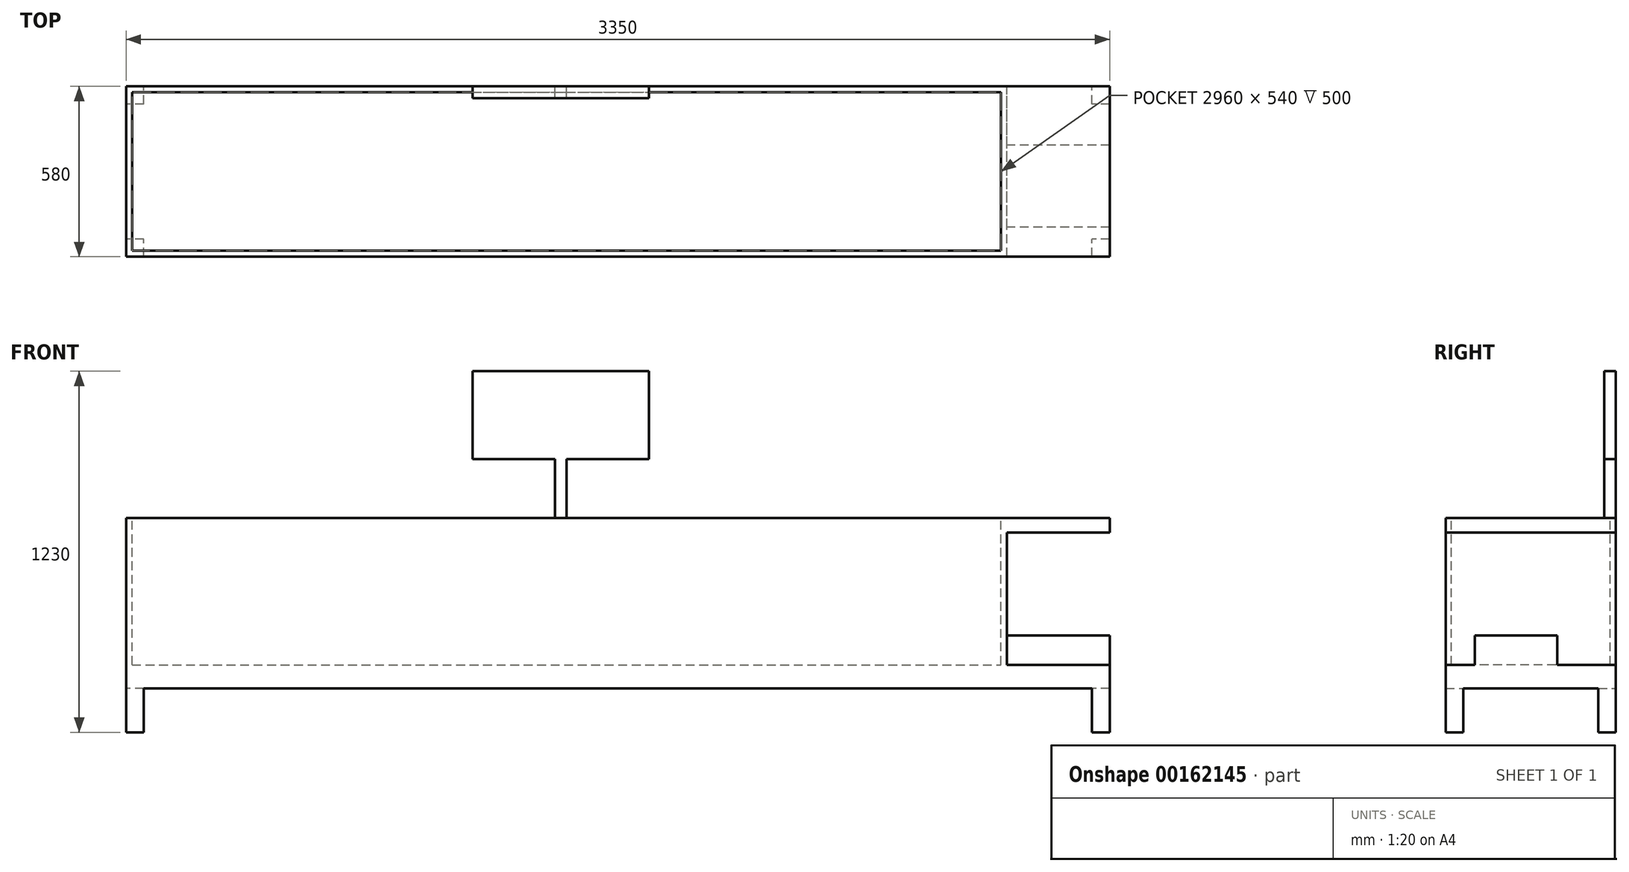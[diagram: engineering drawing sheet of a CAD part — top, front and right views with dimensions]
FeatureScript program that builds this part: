
annotation { "Feature Type Name" : "Feature", "Feature Type Description" : "" }
export const myFeature = defineFeature(function(context is Context, id is Id, definition is map)
    precondition{}
    {
        {
            var Q0;
            Q0=qCreatedBy(makeId("Front.planeOp"),FACE);
            var sketch = newSketch(context, id + "F0", { "sketchPlane" : qUnion([Q0])});
            skLineSegment(sketch, "E0", {"start": v(0, 0) * mm, "end": v(0, 730) * mm});
            skLineSegment(sketch, "E1", {"start": v(0, 730) * mm, "end": v(3350, 730) * mm});
            skLineSegment(sketch, "E2", {"start": v(3350, 730) * mm, "end": v(3350, 680) * mm});
            skLineSegment(sketch, "E3", {"start": v(3350, 680) * mm, "end": v(3000, 680) * mm});
            skLineSegment(sketch, "E4", {"start": v(3000, 680) * mm, "end": v(3000, 330) * mm});
            skLineSegment(sketch, "E5", {"start": v(3000, 330) * mm, "end": v(3350, 330) * mm});
            skLineSegment(sketch, "E6", {"start": v(3350, 330) * mm, "end": v(3350, 0) * mm});
            skLineSegment(sketch, "E7", {"start": v(3350, 0) * mm, "end": v(3290, 0) * mm});
            skLineSegment(sketch, "E8", {"start": v(3290, 0) * mm, "end": v(3290, 150) * mm});
            skLineSegment(sketch, "E9", {"start": v(3290, 150) * mm, "end": v(60, 150) * mm});
            skLineSegment(sketch, "E10", {"start": v(60, 150) * mm, "end": v(60, 0) * mm});
            skLineSegment(sketch, "E11", {"start": v(60, 0) * mm, "end": v(0, 0) * mm});
            skSolve(sketch);
        }
        {
            var Q0;
            Q0 = qSketchRegion(id + "F0", true);
            extrude(context, id + "F1", {"entities" : qUnion([Q0]), "depth" : 580 * mm});
        }
        {
            var Q0;
            Q0=makeQuery(id+"F1.opExtrude","SWEPT_FACE",FACE,{"disambiguationData":[OSD([sQuery(id+"F0.wireOp",EDGE,"E0")])]});
            var sketch = newSketch(context, id + "F2", { "sketchPlane" : qUnion([Q0])});
            skLineSegment(sketch, "E12.bottom", {"start": v(520, 0) * mm, "end": v(60, 0) * mm});
            skLineSegment(sketch, "E12.top", {"start": v(520, 150) * mm, "end": v(60, 150) * mm});
            skLineSegment(sketch, "E12.left", {"start": v(520, 0) * mm, "end": v(520, 150) * mm});
            skLineSegment(sketch, "E12.right", {"start": v(60, 0) * mm, "end": v(60, 150) * mm});
            skSolve(sketch);
        }
        {
            var Q0;
            Q0 = qSketchRegion(id + "F2", true);
            extrude(context, id + "F3", {"entities" : qUnion([Q0]), "operationType" : NewBodyOperationType.REMOVE, "endBound" : BoundingType.THROUGH_ALL, "oppositeDirection" : true, "depth" : 25 * mm});
        }
        {
            var Q0;
            Q0=makeQuery(id+"F1.opExtrude","SWEPT_FACE",FACE,{"disambiguationData":[OSD([sQuery(id+"F0.wireOp",EDGE,"E1")])]});
            var sketch = newSketch(context, id + "F4", { "sketchPlane" : qUnion([Q0])});
            skLineSegment(sketch, "E13.bottom", {"start": v(20, -20) * mm, "end": v(2980, -20) * mm});
            skLineSegment(sketch, "E13.top", {"start": v(20, -560) * mm, "end": v(2980, -560) * mm});
            skLineSegment(sketch, "E13.left", {"start": v(20, -20) * mm, "end": v(20, -560) * mm});
            skLineSegment(sketch, "E13.right", {"start": v(2980, -20) * mm, "end": v(2980, -560) * mm});
            skSolve(sketch);
        }
        {
            var Q0;
            Q0 = qSketchRegion(id + "F4", true);
            extrude(context, id + "F5", {"entities" : qUnion([Q0]), "operationType" : NewBodyOperationType.REMOVE, "oppositeDirection" : true, "depth" : 500 * mm});
        }
        {
            var Q0;
            Q0=makeQuery(id+"F1.opExtrude","SWEPT_FACE",FACE,{"disambiguationData":[OSD([sQuery(id+"F0.wireOp",EDGE,"E5")])]});
            var sketch = newSketch(context, id + "F6", { "sketchPlane" : qUnion([Q0])});
            skLineSegment(sketch, "E14.bottom", {"start": v(3350, -580) * mm, "end": v(3000, -580) * mm});
            skLineSegment(sketch, "E14.top", {"start": v(3350, -480) * mm, "end": v(3000, -480) * mm});
            skLineSegment(sketch, "E14.left", {"start": v(3350, -580) * mm, "end": v(3350, -480) * mm});
            skLineSegment(sketch, "E14.right", {"start": v(3000, -580) * mm, "end": v(3000, -480) * mm});
            skLineSegment(sketch, "E15.bottom", {"start": v(3350, 0) * mm, "end": v(3000, 0) * mm});
            skLineSegment(sketch, "E15.top", {"start": v(3350, -200) * mm, "end": v(3000, -200) * mm});
            skLineSegment(sketch, "E15.left", {"start": v(3350, 0) * mm, "end": v(3350, -200) * mm});
            skLineSegment(sketch, "E15.right", {"start": v(3000, 0) * mm, "end": v(3000, -200) * mm});
            skSolve(sketch);
        }
        {
            var Q0;
            Q0 = qSketchRegion(id + "F6", true);
            extrude(context, id + "F7", {"entities" : qUnion([Q0]), "operationType" : NewBodyOperationType.REMOVE, "oppositeDirection" : true, "depth" : 100 * mm});
        }
        {
            var Q0;
            Q0=makeQuery(id+"F1.opExtrude","CAP_FACE",FACE,{"disambiguationData":[OSD([sQuery(id+"F0.wireOp",EDGE,"E0"),sQuery(id+"F0.wireOp",EDGE,"E1"),sQuery(id+"F0.wireOp",EDGE,"E2"),sQuery(id+"F0.wireOp",EDGE,"E3"),sQuery(id+"F0.wireOp",EDGE,"E4"),sQuery(id+"F0.wireOp",EDGE,"E5"),sQuery(id+"F0.wireOp",EDGE,"E6"),sQuery(id+"F0.wireOp",EDGE,"E7"),sQuery(id+"F0.wireOp",EDGE,"E8"),sQuery(id+"F0.wireOp",EDGE,"E9"),sQuery(id+"F0.wireOp",EDGE,"E10"),sQuery(id+"F0.wireOp",EDGE,"E11")])],"isStart":true});
            var sketch = newSketch(context, id + "F8", { "sketchPlane" : qUnion([Q0])});
            skLineSegment(sketch, "E16", {"start": v(-1500, 730) * mm, "end": v(-1500, 930) * mm});
            skLineSegment(sketch, "E17", {"start": v(-1500, 930) * mm, "end": v(-1780, 930) * mm});
            skLineSegment(sketch, "E18", {"start": v(-1780, 930) * mm, "end": v(-1780, 1230) * mm});
            skLineSegment(sketch, "E19", {"start": v(-1780, 1230) * mm, "end": v(-1180, 1230) * mm});
            skLineSegment(sketch, "E20", {"start": v(-1180, 1230) * mm, "end": v(-1180, 930) * mm});
            skLineSegment(sketch, "E21", {"start": v(-1180, 930) * mm, "end": v(-1460, 930) * mm});
            skLineSegment(sketch, "E22", {"start": v(-1460, 930) * mm, "end": v(-1460, 730) * mm});
            skLineSegment(sketch, "E23", {"start": v(-1460, 730) * mm, "end": v(-1500, 730) * mm});
            skSolve(sketch);
        }
        {
            var Q0;
            Q0 = qSketchRegion(id + "F8", true);
            extrude(context, id + "F9", {"entities" : qUnion([Q0]), "operationType" : NewBodyOperationType.ADD, "oppositeDirection" : true, "depth" : 40 * mm});
        }
    });
